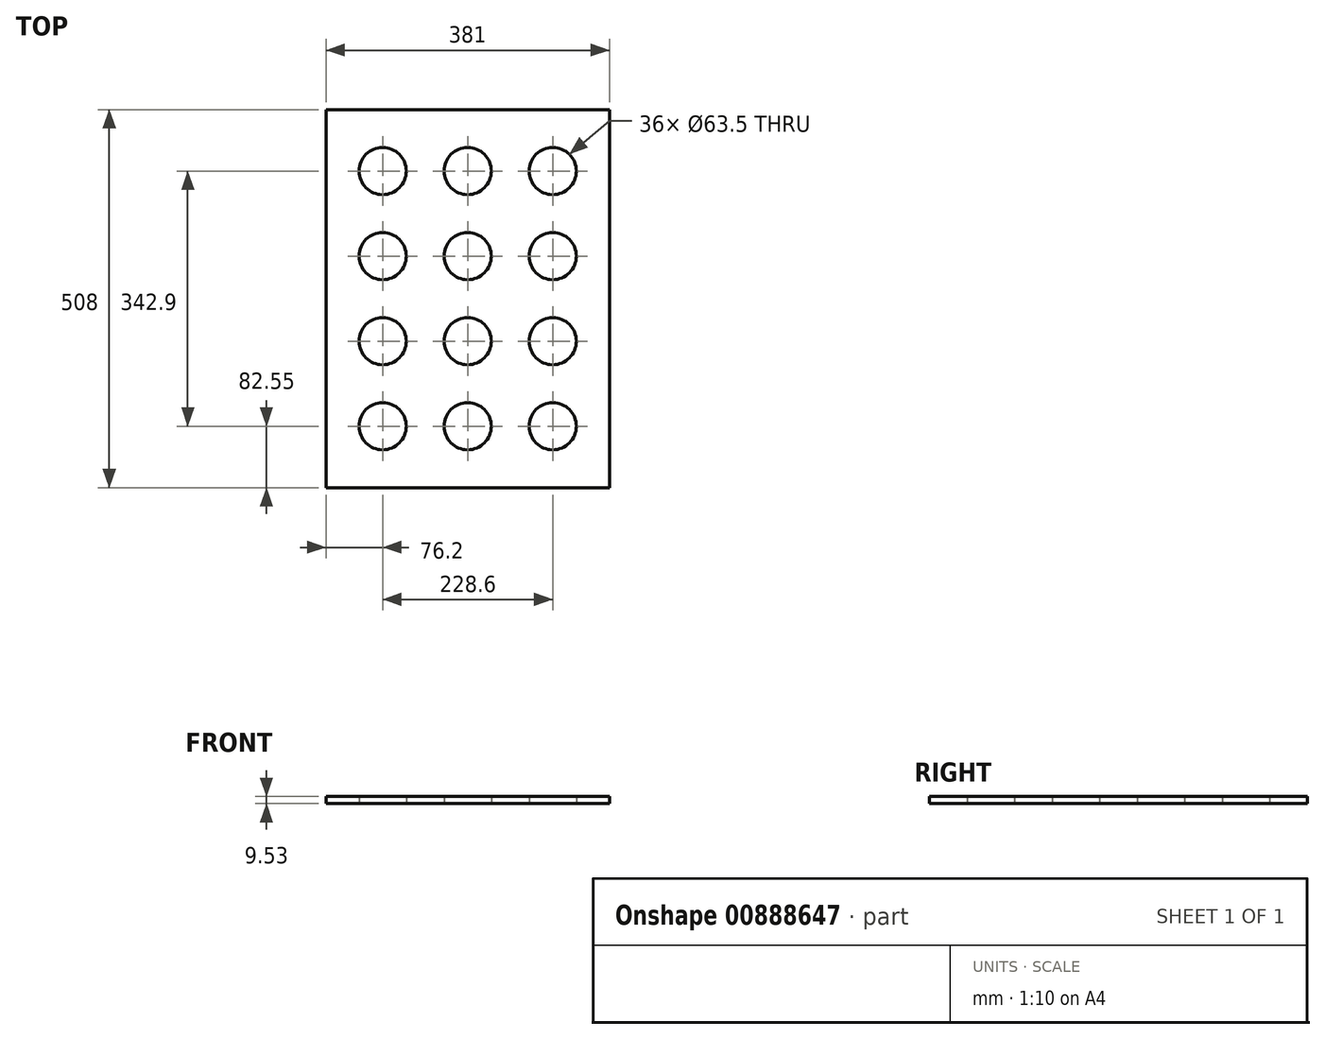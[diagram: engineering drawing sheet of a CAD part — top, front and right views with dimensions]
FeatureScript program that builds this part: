
annotation { "Feature Type Name" : "Feature", "Feature Type Description" : "" }
export const myFeature = defineFeature(function(context is Context, id is Id, definition is map)
    precondition{}
    {
        {
            var Q0;
            Q0=qCreatedBy(makeId("Top.planeOp"),FACE);
            var sketch = newSketch(context, id + "F0", { "sketchPlane" : qUnion([Q0])});
            skCircle(sketch, "E0", {"center": v(-114.3, -171.45) * mm, "radius": 50.8 * mm, "construction": true});
            skCircle(sketch, "E1", {"center": v(-114.3, -171.45) * mm, "radius": 31.75 * mm});
            skCircle(sketch, "E2.0.1.0", {"center": v(-114.3, -57.15) * mm, "radius": 31.75 * mm});
            skCircle(sketch, "E2.0.1.1", {"center": v(-114.3, -57.15) * mm, "radius": 50.8 * mm, "construction": true});
            skCircle(sketch, "E2.0.2.0", {"center": v(-114.3, 57.15) * mm, "radius": 31.75 * mm});
            skCircle(sketch, "E2.0.2.1", {"center": v(-114.3, 57.15) * mm, "radius": 50.8 * mm, "construction": true});
            skCircle(sketch, "E2.0.3.0", {"center": v(-114.3, 171.45) * mm, "radius": 31.75 * mm});
            skCircle(sketch, "E2.0.3.1", {"center": v(-114.3, 171.45) * mm, "radius": 50.8 * mm, "construction": true});
            skCircle(sketch, "E2.1.0.0", {"center": v(0, -171.45) * mm, "radius": 31.75 * mm});
            skCircle(sketch, "E2.1.0.1", {"center": v(0, -171.45) * mm, "radius": 50.8 * mm, "construction": true});
            skCircle(sketch, "E2.1.1.0", {"center": v(0, -57.15) * mm, "radius": 31.75 * mm});
            skCircle(sketch, "E2.1.1.1", {"center": v(0, -57.15) * mm, "radius": 50.8 * mm, "construction": true});
            skCircle(sketch, "E2.1.2.0", {"center": v(0, 57.15) * mm, "radius": 31.75 * mm});
            skCircle(sketch, "E2.1.2.1", {"center": v(0, 57.15) * mm, "radius": 50.8 * mm, "construction": true});
            skCircle(sketch, "E2.1.3.0", {"center": v(0, 171.45) * mm, "radius": 31.75 * mm});
            skCircle(sketch, "E2.1.3.1", {"center": v(0, 171.45) * mm, "radius": 50.8 * mm, "construction": true});
            skCircle(sketch, "E2.2.0.0", {"center": v(114.3, -171.45) * mm, "radius": 31.75 * mm});
            skCircle(sketch, "E2.2.0.1", {"center": v(114.3, -171.45) * mm, "radius": 50.8 * mm, "construction": true});
            skCircle(sketch, "E2.2.1.0", {"center": v(114.3, -57.15) * mm, "radius": 31.75 * mm});
            skCircle(sketch, "E2.2.1.1", {"center": v(114.3, -57.15) * mm, "radius": 50.8 * mm, "construction": true});
            skCircle(sketch, "E2.2.2.0", {"center": v(114.3, 57.15) * mm, "radius": 31.75 * mm});
            skCircle(sketch, "E2.2.2.1", {"center": v(114.3, 57.15) * mm, "radius": 50.8 * mm, "construction": true});
            skCircle(sketch, "E2.2.3.0", {"center": v(114.3, 171.45) * mm, "radius": 31.75 * mm});
            skCircle(sketch, "E2.2.3.1", {"center": v(114.3, 171.45) * mm, "radius": 50.8 * mm, "construction": true});
            skLineSegment(sketch, "E2.direction1", {"start": v(-114.3, -171.45) * mm, "end": v(0, -171.45) * mm, "construction": true});
            skLineSegment(sketch, "E2.direction2", {"start": v(-114.3, -171.45) * mm, "end": v(-114.3, -57.15) * mm, "construction": true});
            skLineSegment(sketch, "E3.bottom", {"start": v(-190.5, 254) * mm, "end": v(190.5, 254) * mm});
            skLineSegment(sketch, "E3.top", {"start": v(-190.5, -254) * mm, "end": v(190.5, -254) * mm});
            skLineSegment(sketch, "E3.left", {"start": v(-190.5, 254) * mm, "end": v(-190.5, -254) * mm});
            skLineSegment(sketch, "E3.right", {"start": v(190.5, 254) * mm, "end": v(190.5, -254) * mm});
            skLineSegment(sketch, "E4", {"start": v(-190.5, 254) * mm, "end": v(190.5, -254) * mm, "construction": true});
            skLineSegment(sketch, "E5", {"start": v(114.3, -171.45) * mm, "end": v(-114.3, 171.45) * mm});
            skSolve(sketch);
        }
        {
            var Q0;
            Q0=qSketchRegion(id+"F0",true);
            extrude(context, id + "F1", {"entities" : qUnion([Q0]), "depth" : 9.52 * mm, "offsetDistance" : 25.4 * mm});
        }
    });
